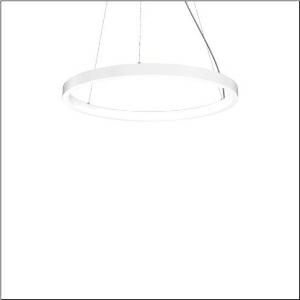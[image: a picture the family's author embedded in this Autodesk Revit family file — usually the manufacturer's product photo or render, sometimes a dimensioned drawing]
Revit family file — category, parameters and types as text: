
# Revit family: silica_r__21_ring-i_5pjbi3d3004a_ea64
name_source: partatom
category: Lighting Fixtures
units: mm (PartAtom-declared; Revit-internal decimal feet)

## family parameters
Cut with Voids When Loaded = No
Host = Face
Light Source = No
Part Type = Normal
Room Calculation Point = No
Round Connector Dimension = Use Diameter
Shared = No

## types (1)
- Silica® 21 Ring-I (1 x LED, 6430 lm, 105 W, 4000K)
    Apparent Load = 105 VA
    CIE Flux Codes = 22 48 76 50 101
    Color Rendering = 80
    Color Temperature = 4000K
    Default Elevation = 1800 mm
    Description = Silica® 21 Ring-I, suspended luminaire, of PMMA, frosted, light emission: inner ring side luminous distribution, primary light characteristic: symmetric, installation type: suspended mounting, LED, rated luminous flux: 6.430lm, luminous efficacy: 61lm/W, light colour: 840, colour temperature: 4000K, control gear: DALI 2, with terminal, 5-pole, mains connection: 230V, AC/DC, 0/50..60Hz, rated input power: 105W, housing, of extruded aluminium section, traffic white (RAL 9016), diameter: 1.090mm, ceiling canopy, traffic white (RAL 9016), protection rating (lamp compartment): IP40, insulation class (complete): insulation class I (protective earthing), certification: CE, impact resistance: IK02, permissible operating ambient temperature: 0..+35°C, packaging unit: 1 piece
    Height = 48 mm  [stored 0.15748 ft]
    Lamp = 1 x LED
    Lamp Light Flux = 6430 lm
    Lamp Power = 105 W
    Lamp count = 1
    Length = 1090 mm
    Luminous efficacy = 61 lm/W
    Manufacturer = Siteco
    ModVariant = No
    Model = 5PJBI3D3004A
    Mounting Place = Ceiling
    Mounting Type = Pendant
    Number of Poles = 1
    OnlyDefault = Yes
    Power Factor = 1
    Product Name = Silica® 21 Ring-I
    Product group = suspended luminaire
    ProductGroupID = 905
    Protection Class = Protection class I
    Protection Degree = IP 40
    RLX_Detail_Level = 1
    RLX_Emergency_Light_Flux = 0 lm
    RLX_Emergency_Type = 0
    RLX_Emergency_Type_DB = No
    RlxData = <blob elided: 12809 chars, md5=b03c5e8a>
    Socket = socket
    Standby Power = 0 W
    System Light Flux = 6430 lm
    System Power = 105 W
    Type Comments = Product without accessories
    Type Image = l_1258371.jpg
    URL = http://relux.com
    VarID = ---
    Voltage = 0 V
    Weight = 0.00 kg
    Width = 0 mm  [stored 0 ft]

note: [stored X ft] marks values corroborated as IEEE doubles in the binary element streams (Revit-internal decimal feet)

## geometry (parser evidence)
native form markers: Sweep x9
no freeform markers — native parametric forms only
